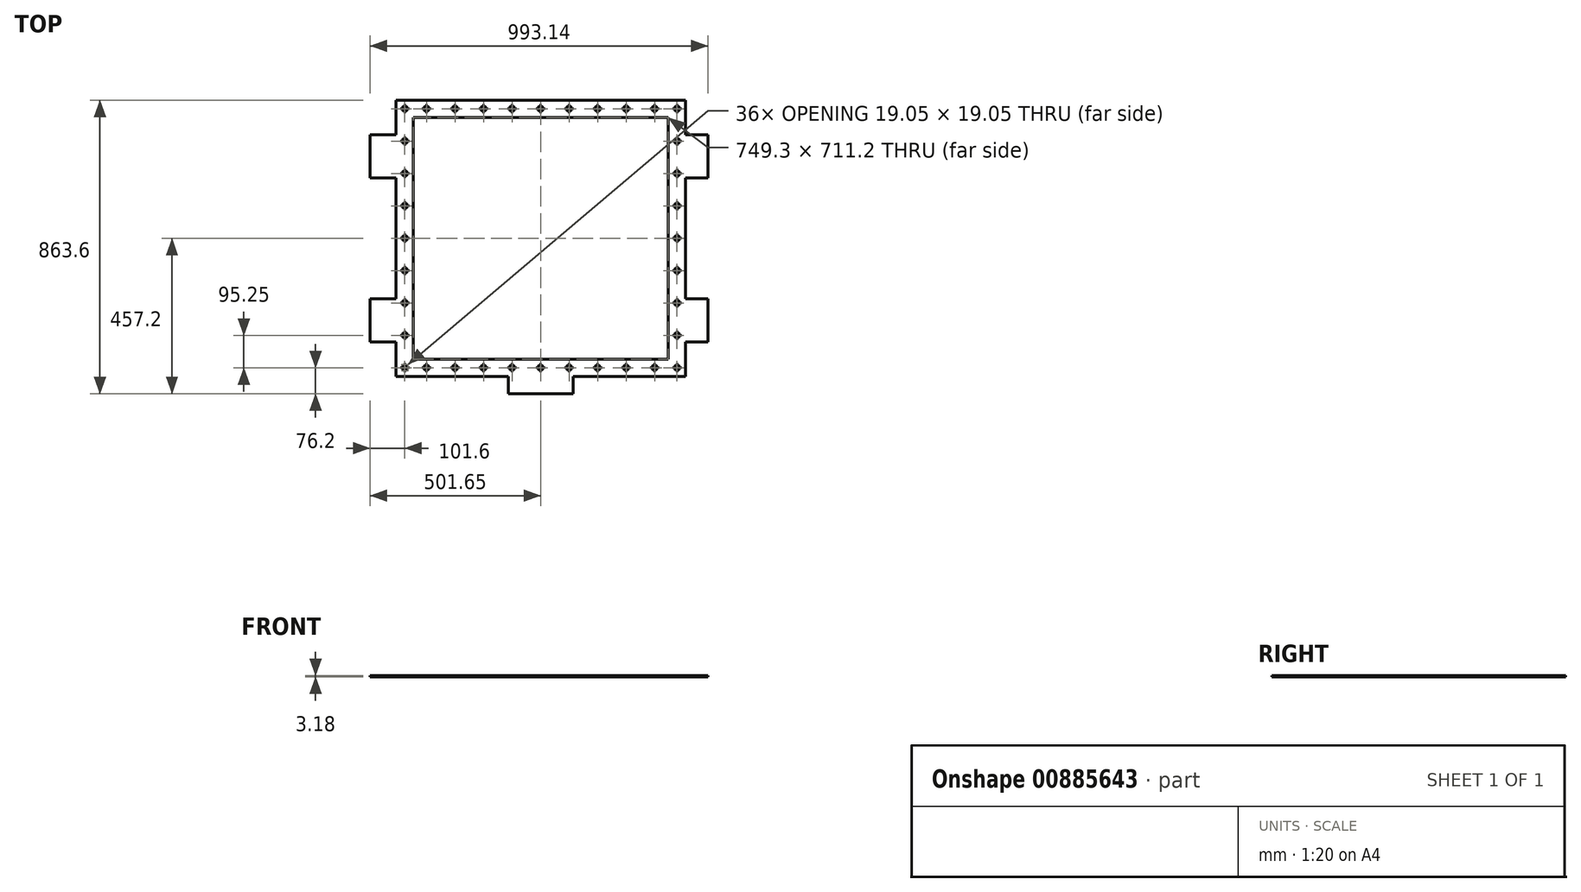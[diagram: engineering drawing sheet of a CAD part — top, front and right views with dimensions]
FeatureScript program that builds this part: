
annotation { "Feature Type Name" : "Feature", "Feature Type Description" : "" }
export const myFeature = defineFeature(function(context is Context, id is Id, definition is map)
    precondition{}
    {
        {
            var Q0;
            Q0=qCreatedBy(makeId("Top.planeOp"),FACE);
            var sketch = newSketch(context, id + "F0", { "sketchPlane" : qUnion([Q0])});
            skLineSegment(sketch, "E0.bottom", {"start": v(374.65, 355.6) * mm, "end": v(-374.65, 355.6) * mm});
            skLineSegment(sketch, "E0.top", {"start": v(374.65, -355.6) * mm, "end": v(-374.65, -355.6) * mm});
            skLineSegment(sketch, "E0.left", {"start": v(374.65, 355.6) * mm, "end": v(374.65, -355.6) * mm});
            skLineSegment(sketch, "E0.right", {"start": v(-374.65, 355.6) * mm, "end": v(-374.65, -355.6) * mm});
            skPoint(sketch, "E0.middle", {"position": v(0, 0) * mm});
            skLineSegment(sketch, "E1.bottom", {"start": v(425.45, 406.4) * mm, "end": v(-425.45, 406.4) * mm});
            skLineSegment(sketch, "E1.top", {"start": v(425.45, -406.4) * mm, "end": v(95.25, -406.4) * mm});
            skLineSegment(sketch, "E1.left", {"start": v(425.45, 406.4) * mm, "end": v(425.45, 304.8) * mm});
            skLineSegment(sketch, "E1.right", {"start": v(-425.45, 406.4) * mm, "end": v(-425.45, 304.8) * mm});
            skLineSegment(sketch, "E2.bottom", {"start": v(-425.45, 304.8) * mm, "end": v(-501.65, 304.8) * mm});
            skLineSegment(sketch, "E2.top", {"start": v(-425.45, 177.8) * mm, "end": v(-501.65, 177.8) * mm});
            skLineSegment(sketch, "E2.right", {"start": v(-501.65, 304.8) * mm, "end": v(-501.65, 177.8) * mm});
            skLineSegment(sketch, "E3.bottom", {"start": v(-425.45, -177.8) * mm, "end": v(-501.65, -177.8) * mm});
            skLineSegment(sketch, "E3.top", {"start": v(-425.45, -304.8) * mm, "end": v(-501.65, -304.8) * mm});
            skLineSegment(sketch, "E3.right", {"start": v(-501.65, -177.8) * mm, "end": v(-501.65, -304.8) * mm});
            skLineSegment(sketch, "E4.trimOffspring", {"start": v(-425.45, 177.8) * mm, "end": v(-425.45, -177.8) * mm});
            skLineSegment(sketch, "E5.trimOffspring", {"start": v(-425.45, -304.8) * mm, "end": v(-425.45, -406.4) * mm});
            skLineSegment(sketch, "E6.bottom", {"start": v(425.45, 304.8) * mm, "end": v(491.5, 304.8) * mm});
            skLineSegment(sketch, "E6.top", {"start": v(425.45, 177.8) * mm, "end": v(491.5, 177.8) * mm});
            skLineSegment(sketch, "E6.right", {"start": v(491.5, 304.8) * mm, "end": v(491.5, 177.8) * mm});
            skLineSegment(sketch, "E7.bottom", {"start": v(425.45, -177.8) * mm, "end": v(491.5, -177.8) * mm});
            skLineSegment(sketch, "E7.top", {"start": v(425.45, -304.8) * mm, "end": v(491.5, -304.8) * mm});
            skLineSegment(sketch, "E7.right", {"start": v(491.5, -177.8) * mm, "end": v(491.5, -304.8) * mm});
            skLineSegment(sketch, "E8.trimOffspring", {"start": v(425.45, 177.8) * mm, "end": v(425.45, -177.8) * mm});
            skLineSegment(sketch, "E9.trimOffspring", {"start": v(425.45, -304.8) * mm, "end": v(425.45, -406.4) * mm});
            skLineSegment(sketch, "E10.top", {"start": v(95.25, -457.2) * mm, "end": v(-95.25, -457.2) * mm});
            skLineSegment(sketch, "E10.left", {"start": v(95.25, -406.4) * mm, "end": v(95.25, -457.2) * mm});
            skLineSegment(sketch, "E10.right", {"start": v(-95.25, -406.4) * mm, "end": v(-95.25, -457.2) * mm});
            skPoint(sketch, "E10.middle", {"position": v(0, -431.8) * mm});
            skLineSegment(sketch, "E11.trimOffspring", {"start": v(-95.25, -406.4) * mm, "end": v(-425.45, -406.4) * mm});
            skSolve(sketch);
        }
        {
            var Q0;
            Q0=makeQuery(id+"F0.imprint","IMPRINT",FACE,{"disambiguationData":[TD([[makeQuery(id+"F0.imprint","IMPRINT",EDGE,{"derivedFrom":sQuery(id+"F0.wireOp",EDGE,"E0.bottom")}),-1.0]])]});
            extrude(context, id + "F1", {"entities" : qUnion([Q0]), "depth" : 3.17 * mm, "offsetDistance" : 25.4 * mm});
        }
        {
            var Q0;
            Q0=makeQuery(id+"F1.opExtrude","CAP_FACE",FACE,{"disambiguationData":[OSD([sQuery(id+"F0.wireOp",EDGE,"E0.bottom"),sQuery(id+"F0.wireOp",EDGE,"E0.top"),sQuery(id+"F0.wireOp",EDGE,"E0.left"),sQuery(id+"F0.wireOp",EDGE,"E0.right"),sQuery(id+"F0.wireOp",EDGE,"E1.bottom"),sQuery(id+"F0.wireOp",EDGE,"E1.top"),sQuery(id+"F0.wireOp",EDGE,"E1.left"),sQuery(id+"F0.wireOp",EDGE,"E1.right"),sQuery(id+"F0.wireOp",EDGE,"E2.bottom"),sQuery(id+"F0.wireOp",EDGE,"E2.top"),sQuery(id+"F0.wireOp",EDGE,"E2.right"),sQuery(id+"F0.wireOp",EDGE,"E3.bottom"),sQuery(id+"F0.wireOp",EDGE,"E3.top"),sQuery(id+"F0.wireOp",EDGE,"E3.right"),sQuery(id+"F0.wireOp",EDGE,"E4.trimOffspring"),sQuery(id+"F0.wireOp",EDGE,"E5.trimOffspring"),sQuery(id+"F0.wireOp",EDGE,"E6.bottom"),sQuery(id+"F0.wireOp",EDGE,"E6.top"),sQuery(id+"F0.wireOp",EDGE,"E6.right"),sQuery(id+"F0.wireOp",EDGE,"E7.bottom"),sQuery(id+"F0.wireOp",EDGE,"E7.top"),sQuery(id+"F0.wireOp",EDGE,"E7.right"),sQuery(id+"F0.wireOp",EDGE,"E8.trimOffspring"),sQuery(id+"F0.wireOp",EDGE,"E9.trimOffspring"),sQuery(id+"F0.wireOp",EDGE,"E10.top"),sQuery(id+"F0.wireOp",EDGE,"E10.left"),sQuery(id+"F0.wireOp",EDGE,"E10.right"),sQuery(id+"F0.wireOp",EDGE,"E11.trimOffspring")])],"isStart":false});
            var sketch = newSketch(context, id + "F2", { "sketchPlane" : qUnion([Q0])});
            skLineSegment(sketch, "E12", {"start": v(-400.05, 406.4) * mm, "end": v(-400.05, -406.4) * mm, "construction": true});
            skLineSegment(sketch, "E13", {"start": v(-425.45, 0) * mm, "end": v(425.45, 0) * mm, "construction": true});
            skLineSegment(sketch, "E14.bottom", {"start": v(-396.88, 9.52) * mm, "end": v(-403.23, 9.52) * mm});
            skLineSegment(sketch, "E14.top", {"start": v(-396.88, -9.53) * mm, "end": v(-403.23, -9.53) * mm});
            skLineSegment(sketch, "E14.left", {"start": v(-396.88, 9.52) * mm, "end": v(-396.88, 3.17) * mm});
            skLineSegment(sketch, "E14.right", {"start": v(-403.23, 9.52) * mm, "end": v(-403.23, 3.17) * mm});
            skPoint(sketch, "E14.middle", {"position": v(-400.05, 0) * mm});
            skLineSegment(sketch, "E15.bottom", {"start": v(-390.53, 3.17) * mm, "end": v(-396.88, 3.17) * mm});
            skLineSegment(sketch, "E15.top", {"start": v(-390.53, -3.18) * mm, "end": v(-396.88, -3.18) * mm});
            skLineSegment(sketch, "E15.left", {"start": v(-390.53, 3.17) * mm, "end": v(-390.53, -3.18) * mm});
            skLineSegment(sketch, "E15.right", {"start": v(-409.58, 3.17) * mm, "end": v(-409.58, -3.18) * mm});
            skLineSegment(sketch, "E16.trimOffspring", {"start": v(-403.23, 3.17) * mm, "end": v(-409.58, 3.17) * mm});
            skLineSegment(sketch, "E17.trimOffspring", {"start": v(-403.23, -3.18) * mm, "end": v(-403.23, -9.53) * mm});
            skLineSegment(sketch, "E18.trimOffspring", {"start": v(-396.88, -3.18) * mm, "end": v(-396.88, -9.53) * mm});
            skLineSegment(sketch, "E19.trimOffspring", {"start": v(-403.23, -3.18) * mm, "end": v(-409.58, -3.18) * mm});
            skLineSegment(sketch, "E20.0.1.0", {"start": v(-396.88, 92.07) * mm, "end": v(-396.88, 85.72) * mm});
            skLineSegment(sketch, "E20.0.1.1", {"start": v(-390.53, 92.07) * mm, "end": v(-396.88, 92.07) * mm});
            skLineSegment(sketch, "E20.0.1.2", {"start": v(-390.53, 98.42) * mm, "end": v(-396.88, 98.42) * mm});
            skLineSegment(sketch, "E20.0.1.3", {"start": v(-390.53, 98.42) * mm, "end": v(-390.53, 92.07) * mm});
            skLineSegment(sketch, "E20.0.1.4", {"start": v(-403.23, 92.07) * mm, "end": v(-403.23, 85.72) * mm});
            skLineSegment(sketch, "E20.0.1.5", {"start": v(-403.23, 92.07) * mm, "end": v(-409.58, 92.07) * mm});
            skLineSegment(sketch, "E20.0.1.6", {"start": v(-409.58, 98.42) * mm, "end": v(-409.58, 92.07) * mm});
            skPoint(sketch, "E20.0.1.7", {"position": v(-400.05, 95.25) * mm});
            skLineSegment(sketch, "E20.0.1.8", {"start": v(-403.23, 98.42) * mm, "end": v(-409.58, 98.42) * mm});
            skLineSegment(sketch, "E20.0.1.9", {"start": v(-396.88, 85.72) * mm, "end": v(-403.23, 85.72) * mm});
            skPoint(sketch, "E20.0.1.10", {"position": v(-400.05, 95.25) * mm});
            skLineSegment(sketch, "E20.0.1.11", {"start": v(-403.23, 104.77) * mm, "end": v(-403.23, 98.42) * mm});
            skLineSegment(sketch, "E20.0.1.12", {"start": v(-396.88, 104.77) * mm, "end": v(-403.23, 104.77) * mm});
            skLineSegment(sketch, "E20.0.1.13", {"start": v(-396.88, 104.77) * mm, "end": v(-396.88, 98.42) * mm});
            skLineSegment(sketch, "E20.0.2.0", {"start": v(-396.88, 187.32) * mm, "end": v(-396.88, 180.97) * mm});
            skLineSegment(sketch, "E20.0.2.1", {"start": v(-390.53, 187.32) * mm, "end": v(-396.88, 187.32) * mm});
            skLineSegment(sketch, "E20.0.2.2", {"start": v(-390.53, 193.67) * mm, "end": v(-396.88, 193.67) * mm});
            skLineSegment(sketch, "E20.0.2.3", {"start": v(-390.53, 193.67) * mm, "end": v(-390.53, 187.32) * mm});
            skLineSegment(sketch, "E20.0.2.4", {"start": v(-403.23, 187.32) * mm, "end": v(-403.23, 180.97) * mm});
            skLineSegment(sketch, "E20.0.2.5", {"start": v(-403.23, 187.32) * mm, "end": v(-409.58, 187.32) * mm});
            skLineSegment(sketch, "E20.0.2.6", {"start": v(-409.58, 193.67) * mm, "end": v(-409.58, 187.32) * mm});
            skPoint(sketch, "E20.0.2.7", {"position": v(-400.05, 190.5) * mm});
            skLineSegment(sketch, "E20.0.2.8", {"start": v(-403.23, 193.67) * mm, "end": v(-409.58, 193.67) * mm});
            skLineSegment(sketch, "E20.0.2.9", {"start": v(-396.88, 180.97) * mm, "end": v(-403.23, 180.97) * mm});
            skPoint(sketch, "E20.0.2.10", {"position": v(-400.05, 190.5) * mm});
            skLineSegment(sketch, "E20.0.2.11", {"start": v(-403.23, 200.02) * mm, "end": v(-403.23, 193.67) * mm});
            skLineSegment(sketch, "E20.0.2.12", {"start": v(-396.88, 200.02) * mm, "end": v(-403.23, 200.02) * mm});
            skLineSegment(sketch, "E20.0.2.13", {"start": v(-396.88, 200.02) * mm, "end": v(-396.88, 193.67) * mm});
            skLineSegment(sketch, "E20.0.3.0", {"start": v(-396.88, 282.57) * mm, "end": v(-396.88, 276.22) * mm});
            skLineSegment(sketch, "E20.0.3.1", {"start": v(-390.53, 282.57) * mm, "end": v(-396.88, 282.57) * mm});
            skLineSegment(sketch, "E20.0.3.2", {"start": v(-390.53, 288.92) * mm, "end": v(-396.88, 288.92) * mm});
            skLineSegment(sketch, "E20.0.3.3", {"start": v(-390.53, 288.92) * mm, "end": v(-390.53, 282.57) * mm});
            skLineSegment(sketch, "E20.0.3.4", {"start": v(-403.23, 282.57) * mm, "end": v(-403.23, 276.22) * mm});
            skLineSegment(sketch, "E20.0.3.5", {"start": v(-403.23, 282.57) * mm, "end": v(-409.58, 282.57) * mm});
            skLineSegment(sketch, "E20.0.3.6", {"start": v(-409.58, 288.92) * mm, "end": v(-409.58, 282.57) * mm});
            skPoint(sketch, "E20.0.3.7", {"position": v(-400.05, 285.75) * mm});
            skLineSegment(sketch, "E20.0.3.8", {"start": v(-403.23, 288.92) * mm, "end": v(-409.58, 288.92) * mm});
            skLineSegment(sketch, "E20.0.3.9", {"start": v(-396.88, 276.22) * mm, "end": v(-403.23, 276.22) * mm});
            skPoint(sketch, "E20.0.3.10", {"position": v(-400.05, 285.75) * mm});
            skLineSegment(sketch, "E20.0.3.11", {"start": v(-403.23, 295.27) * mm, "end": v(-403.23, 288.92) * mm});
            skLineSegment(sketch, "E20.0.3.12", {"start": v(-396.88, 295.27) * mm, "end": v(-403.23, 295.27) * mm});
            skLineSegment(sketch, "E20.0.3.13", {"start": v(-396.88, 295.27) * mm, "end": v(-396.88, 288.92) * mm});
            skLineSegment(sketch, "E20.0.4.0", {"start": v(-396.88, 377.82) * mm, "end": v(-396.88, 371.47) * mm});
            skLineSegment(sketch, "E20.0.4.1", {"start": v(-390.53, 377.82) * mm, "end": v(-396.88, 377.82) * mm});
            skLineSegment(sketch, "E20.0.4.2", {"start": v(-390.53, 384.17) * mm, "end": v(-396.88, 384.17) * mm});
            skLineSegment(sketch, "E20.0.4.3", {"start": v(-390.53, 384.17) * mm, "end": v(-390.53, 377.82) * mm});
            skLineSegment(sketch, "E20.0.4.4", {"start": v(-403.23, 377.82) * mm, "end": v(-403.23, 371.47) * mm});
            skLineSegment(sketch, "E20.0.4.5", {"start": v(-403.23, 377.82) * mm, "end": v(-409.58, 377.82) * mm});
            skLineSegment(sketch, "E20.0.4.6", {"start": v(-409.58, 384.17) * mm, "end": v(-409.58, 377.82) * mm});
            skPoint(sketch, "E20.0.4.7", {"position": v(-400.05, 381) * mm});
            skLineSegment(sketch, "E20.0.4.8", {"start": v(-403.23, 384.17) * mm, "end": v(-409.58, 384.17) * mm});
            skLineSegment(sketch, "E20.0.4.9", {"start": v(-396.88, 371.47) * mm, "end": v(-403.23, 371.47) * mm});
            skPoint(sketch, "E20.0.4.10", {"position": v(-400.05, 381) * mm});
            skLineSegment(sketch, "E20.0.4.11", {"start": v(-403.23, 390.52) * mm, "end": v(-403.23, 384.17) * mm});
            skLineSegment(sketch, "E20.0.4.12", {"start": v(-396.88, 390.52) * mm, "end": v(-403.23, 390.52) * mm});
            skLineSegment(sketch, "E20.0.4.13", {"start": v(-396.88, 390.52) * mm, "end": v(-396.88, 384.17) * mm});
            skLineSegment(sketch, "E20.direction1", {"start": v(-403.23, -9.53) * mm, "end": v(-403.23, -9.53) * mm});
            skLineSegment(sketch, "E20.direction2", {"start": v(-403.23, -9.53) * mm, "end": v(-403.23, 85.72) * mm, "construction": true});
            skLineSegment(sketch, "E21.0.1.0", {"start": v(-403.23, -92.08) * mm, "end": v(-409.58, -92.08) * mm});
            skLineSegment(sketch, "E21.0.1.1", {"start": v(-409.58, -92.08) * mm, "end": v(-409.58, -98.43) * mm});
            skLineSegment(sketch, "E21.0.1.2", {"start": v(-403.23, -98.43) * mm, "end": v(-403.23, -104.78) * mm});
            skLineSegment(sketch, "E21.0.1.3", {"start": v(-396.88, -98.43) * mm, "end": v(-396.88, -104.78) * mm});
            skLineSegment(sketch, "E21.0.1.4", {"start": v(-390.53, -92.08) * mm, "end": v(-396.88, -92.08) * mm});
            skLineSegment(sketch, "E21.0.1.5", {"start": v(-390.53, -98.43) * mm, "end": v(-396.88, -98.43) * mm});
            skLineSegment(sketch, "E21.0.1.6", {"start": v(-390.53, -92.08) * mm, "end": v(-390.53, -98.43) * mm});
            skLineSegment(sketch, "E21.0.1.7", {"start": v(-403.23, -98.43) * mm, "end": v(-409.58, -98.43) * mm});
            skLineSegment(sketch, "E21.0.1.8", {"start": v(-396.88, -85.73) * mm, "end": v(-403.23, -85.73) * mm});
            skLineSegment(sketch, "E21.0.1.9", {"start": v(-396.88, -104.78) * mm, "end": v(-403.23, -104.78) * mm});
            skLineSegment(sketch, "E21.0.1.10", {"start": v(-396.88, -85.73) * mm, "end": v(-396.88, -92.08) * mm});
            skLineSegment(sketch, "E21.0.1.11", {"start": v(-403.23, -85.73) * mm, "end": v(-403.23, -92.08) * mm});
            skPoint(sketch, "E21.0.1.12", {"position": v(-400.05, -95.25) * mm});
            skPoint(sketch, "E21.0.1.13", {"position": v(-400.05, -95.25) * mm});
            skLineSegment(sketch, "E21.0.2.0", {"start": v(-403.23, -187.33) * mm, "end": v(-409.58, -187.33) * mm});
            skLineSegment(sketch, "E21.0.2.1", {"start": v(-409.58, -187.33) * mm, "end": v(-409.58, -193.68) * mm});
            skLineSegment(sketch, "E21.0.2.2", {"start": v(-403.23, -193.68) * mm, "end": v(-403.23, -200.03) * mm});
            skLineSegment(sketch, "E21.0.2.3", {"start": v(-396.88, -193.68) * mm, "end": v(-396.88, -200.03) * mm});
            skLineSegment(sketch, "E21.0.2.4", {"start": v(-390.53, -187.33) * mm, "end": v(-396.88, -187.33) * mm});
            skLineSegment(sketch, "E21.0.2.5", {"start": v(-390.53, -193.68) * mm, "end": v(-396.88, -193.68) * mm});
            skLineSegment(sketch, "E21.0.2.6", {"start": v(-390.53, -187.33) * mm, "end": v(-390.53, -193.68) * mm});
            skLineSegment(sketch, "E21.0.2.7", {"start": v(-403.23, -193.68) * mm, "end": v(-409.58, -193.68) * mm});
            skLineSegment(sketch, "E21.0.2.8", {"start": v(-396.88, -180.98) * mm, "end": v(-403.23, -180.98) * mm});
            skLineSegment(sketch, "E21.0.2.9", {"start": v(-396.88, -200.03) * mm, "end": v(-403.23, -200.03) * mm});
            skLineSegment(sketch, "E21.0.2.10", {"start": v(-396.88, -180.98) * mm, "end": v(-396.88, -187.33) * mm});
            skLineSegment(sketch, "E21.0.2.11", {"start": v(-403.23, -180.98) * mm, "end": v(-403.23, -187.33) * mm});
            skPoint(sketch, "E21.0.2.12", {"position": v(-400.05, -190.5) * mm});
            skPoint(sketch, "E21.0.2.13", {"position": v(-400.05, -190.5) * mm});
            skLineSegment(sketch, "E21.0.3.0", {"start": v(-403.23, -282.58) * mm, "end": v(-409.58, -282.58) * mm});
            skLineSegment(sketch, "E21.0.3.1", {"start": v(-409.58, -282.58) * mm, "end": v(-409.58, -288.93) * mm});
            skLineSegment(sketch, "E21.0.3.2", {"start": v(-403.23, -288.93) * mm, "end": v(-403.23, -295.28) * mm});
            skLineSegment(sketch, "E21.0.3.3", {"start": v(-396.88, -288.93) * mm, "end": v(-396.88, -295.28) * mm});
            skLineSegment(sketch, "E21.0.3.4", {"start": v(-390.53, -282.58) * mm, "end": v(-396.88, -282.58) * mm});
            skLineSegment(sketch, "E21.0.3.5", {"start": v(-390.53, -288.93) * mm, "end": v(-396.88, -288.93) * mm});
            skLineSegment(sketch, "E21.0.3.6", {"start": v(-390.53, -282.58) * mm, "end": v(-390.53, -288.93) * mm});
            skLineSegment(sketch, "E21.0.3.7", {"start": v(-403.23, -288.93) * mm, "end": v(-409.58, -288.93) * mm});
            skLineSegment(sketch, "E21.0.3.8", {"start": v(-396.88, -276.23) * mm, "end": v(-403.23, -276.23) * mm});
            skLineSegment(sketch, "E21.0.3.9", {"start": v(-396.88, -295.28) * mm, "end": v(-403.23, -295.28) * mm});
            skLineSegment(sketch, "E21.0.3.10", {"start": v(-396.88, -276.23) * mm, "end": v(-396.88, -282.58) * mm});
            skLineSegment(sketch, "E21.0.3.11", {"start": v(-403.23, -276.23) * mm, "end": v(-403.23, -282.58) * mm});
            skPoint(sketch, "E21.0.3.12", {"position": v(-400.05, -285.75) * mm});
            skPoint(sketch, "E21.0.3.13", {"position": v(-400.05, -285.75) * mm});
            skLineSegment(sketch, "E21.0.4.0", {"start": v(-403.23, -377.83) * mm, "end": v(-409.58, -377.83) * mm});
            skLineSegment(sketch, "E21.0.4.1", {"start": v(-409.58, -377.83) * mm, "end": v(-409.58, -384.18) * mm});
            skLineSegment(sketch, "E21.0.4.2", {"start": v(-403.23, -384.18) * mm, "end": v(-403.23, -390.53) * mm});
            skLineSegment(sketch, "E21.0.4.3", {"start": v(-396.88, -384.18) * mm, "end": v(-396.88, -390.53) * mm});
            skLineSegment(sketch, "E21.0.4.4", {"start": v(-390.53, -377.83) * mm, "end": v(-396.88, -377.83) * mm});
            skLineSegment(sketch, "E21.0.4.5", {"start": v(-390.53, -384.18) * mm, "end": v(-396.88, -384.18) * mm});
            skLineSegment(sketch, "E21.0.4.6", {"start": v(-390.53, -377.83) * mm, "end": v(-390.53, -384.18) * mm});
            skLineSegment(sketch, "E21.0.4.7", {"start": v(-403.23, -384.18) * mm, "end": v(-409.58, -384.18) * mm});
            skLineSegment(sketch, "E21.0.4.8", {"start": v(-396.88, -371.48) * mm, "end": v(-403.23, -371.48) * mm});
            skLineSegment(sketch, "E21.0.4.9", {"start": v(-396.88, -390.53) * mm, "end": v(-403.23, -390.53) * mm});
            skLineSegment(sketch, "E21.0.4.10", {"start": v(-396.88, -371.48) * mm, "end": v(-396.88, -377.83) * mm});
            skLineSegment(sketch, "E21.0.4.11", {"start": v(-403.23, -371.48) * mm, "end": v(-403.23, -377.83) * mm});
            skPoint(sketch, "E21.0.4.12", {"position": v(-400.05, -381) * mm});
            skPoint(sketch, "E21.0.4.13", {"position": v(-400.05, -381) * mm});
            skLineSegment(sketch, "E21.direction1", {"start": v(-403.23, -9.53) * mm, "end": v(-377.83, -9.53) * mm, "construction": true});
            skLineSegment(sketch, "E21.direction2", {"start": v(-403.23, -9.53) * mm, "end": v(-403.23, -104.78) * mm, "construction": true});
            skLineSegment(sketch, "E22", {"start": v(0, -457.2) * mm, "end": v(0, 406.4) * mm, "construction": true});
            skLineSegment(sketch, "E23.0.4.0", {"start": v(-3.36, -377.86) * mm, "end": v(-9.7, -377.86) * mm});
            skLineSegment(sketch, "E23.0.4.1", {"start": v(-9.7, -377.86) * mm, "end": v(-9.7, -384.2) * mm});
            skLineSegment(sketch, "E23.0.4.2", {"start": v(-3.36, -384.2) * mm, "end": v(-3.36, -390.56) * mm});
            skLineSegment(sketch, "E23.0.4.3", {"start": v(3, -384.2) * mm, "end": v(3, -390.56) * mm});
            skLineSegment(sketch, "E23.0.4.4", {"start": v(9.34, -377.86) * mm, "end": v(3, -377.86) * mm});
            skLineSegment(sketch, "E23.0.4.5", {"start": v(9.34, -384.2) * mm, "end": v(3, -384.2) * mm});
            skLineSegment(sketch, "E23.0.4.6", {"start": v(9.34, -377.86) * mm, "end": v(9.34, -384.2) * mm});
            skLineSegment(sketch, "E23.0.4.7", {"start": v(-3.36, -384.2) * mm, "end": v(-9.7, -384.2) * mm});
            skLineSegment(sketch, "E23.0.4.8", {"start": v(3, -371.5) * mm, "end": v(-3.36, -371.5) * mm});
            skLineSegment(sketch, "E23.0.4.9", {"start": v(3, -390.56) * mm, "end": v(-3.36, -390.56) * mm});
            skLineSegment(sketch, "E23.0.4.10", {"start": v(3, -371.5) * mm, "end": v(3, -377.86) * mm});
            skLineSegment(sketch, "E23.0.4.11", {"start": v(-3.36, -371.5) * mm, "end": v(-3.36, -377.86) * mm});
            skPoint(sketch, "E23.0.4.12", {"position": v(-0.18, -381.03) * mm});
            skPoint(sketch, "E23.0.4.13", {"position": v(-0.18, -381.03) * mm});
            skLineSegment(sketch, "E24.1.0.0", {"start": v(80.46, -371.5) * mm, "end": v(80.46, -377.86) * mm});
            skLineSegment(sketch, "E24.1.0.1", {"start": v(93.16, -384.2) * mm, "end": v(86.81, -384.2) * mm});
            skLineSegment(sketch, "E24.1.0.2", {"start": v(86.81, -390.56) * mm, "end": v(80.46, -390.56) * mm});
            skLineSegment(sketch, "E24.1.0.3", {"start": v(86.81, -384.2) * mm, "end": v(86.81, -390.56) * mm});
            skLineSegment(sketch, "E24.1.0.4", {"start": v(93.16, -377.86) * mm, "end": v(86.81, -377.86) * mm});
            skPoint(sketch, "E24.1.0.5", {"position": v(83.64, -381.03) * mm});
            skLineSegment(sketch, "E24.1.0.6", {"start": v(80.46, -384.2) * mm, "end": v(80.46, -390.56) * mm});
            skLineSegment(sketch, "E24.1.0.7", {"start": v(86.81, -371.5) * mm, "end": v(86.81, -377.86) * mm});
            skLineSegment(sketch, "E24.1.0.8", {"start": v(86.81, -371.5) * mm, "end": v(80.46, -371.5) * mm});
            skPoint(sketch, "E24.1.0.9", {"position": v(83.64, -381.03) * mm});
            skLineSegment(sketch, "E24.1.0.10", {"start": v(80.46, -377.86) * mm, "end": v(74.11, -377.86) * mm});
            skLineSegment(sketch, "E24.1.0.11", {"start": v(93.16, -377.86) * mm, "end": v(93.16, -384.2) * mm});
            skLineSegment(sketch, "E24.1.0.12", {"start": v(80.46, -384.2) * mm, "end": v(74.11, -384.2) * mm});
            skLineSegment(sketch, "E24.1.0.13", {"start": v(74.11, -377.86) * mm, "end": v(74.11, -384.2) * mm});
            skLineSegment(sketch, "E24.2.0.0", {"start": v(164.28, -371.5) * mm, "end": v(164.28, -377.86) * mm});
            skLineSegment(sketch, "E24.2.0.1", {"start": v(176.98, -384.2) * mm, "end": v(170.63, -384.2) * mm});
            skLineSegment(sketch, "E24.2.0.2", {"start": v(170.63, -390.56) * mm, "end": v(164.28, -390.56) * mm});
            skLineSegment(sketch, "E24.2.0.3", {"start": v(170.63, -384.2) * mm, "end": v(170.63, -390.56) * mm});
            skLineSegment(sketch, "E24.2.0.4", {"start": v(176.98, -377.86) * mm, "end": v(170.63, -377.86) * mm});
            skPoint(sketch, "E24.2.0.5", {"position": v(167.46, -381.03) * mm});
            skLineSegment(sketch, "E24.2.0.6", {"start": v(164.28, -384.2) * mm, "end": v(164.28, -390.56) * mm});
            skLineSegment(sketch, "E24.2.0.7", {"start": v(170.63, -371.5) * mm, "end": v(170.63, -377.86) * mm});
            skLineSegment(sketch, "E24.2.0.8", {"start": v(170.63, -371.5) * mm, "end": v(164.28, -371.5) * mm});
            skPoint(sketch, "E24.2.0.9", {"position": v(167.46, -381.03) * mm});
            skLineSegment(sketch, "E24.2.0.10", {"start": v(164.28, -377.86) * mm, "end": v(157.93, -377.86) * mm});
            skLineSegment(sketch, "E24.2.0.11", {"start": v(176.98, -377.86) * mm, "end": v(176.98, -384.2) * mm});
            skLineSegment(sketch, "E24.2.0.12", {"start": v(164.28, -384.2) * mm, "end": v(157.93, -384.2) * mm});
            skLineSegment(sketch, "E24.2.0.13", {"start": v(157.93, -377.86) * mm, "end": v(157.93, -384.2) * mm});
            skLineSegment(sketch, "E24.3.0.0", {"start": v(248.1, -371.5) * mm, "end": v(248.1, -377.86) * mm});
            skLineSegment(sketch, "E24.3.0.1", {"start": v(260.8, -384.2) * mm, "end": v(254.45, -384.2) * mm});
            skLineSegment(sketch, "E24.3.0.2", {"start": v(254.45, -390.56) * mm, "end": v(248.1, -390.56) * mm});
            skLineSegment(sketch, "E24.3.0.3", {"start": v(254.45, -384.2) * mm, "end": v(254.45, -390.56) * mm});
            skLineSegment(sketch, "E24.3.0.4", {"start": v(260.8, -377.86) * mm, "end": v(254.45, -377.86) * mm});
            skPoint(sketch, "E24.3.0.5", {"position": v(251.28, -381.03) * mm});
            skLineSegment(sketch, "E24.3.0.6", {"start": v(248.1, -384.2) * mm, "end": v(248.1, -390.56) * mm});
            skLineSegment(sketch, "E24.3.0.7", {"start": v(254.45, -371.5) * mm, "end": v(254.45, -377.86) * mm});
            skLineSegment(sketch, "E24.3.0.8", {"start": v(254.45, -371.5) * mm, "end": v(248.1, -371.5) * mm});
            skPoint(sketch, "E24.3.0.9", {"position": v(251.28, -381.03) * mm});
            skLineSegment(sketch, "E24.3.0.10", {"start": v(248.1, -377.86) * mm, "end": v(241.75, -377.86) * mm});
            skLineSegment(sketch, "E24.3.0.11", {"start": v(260.8, -377.86) * mm, "end": v(260.8, -384.2) * mm});
            skLineSegment(sketch, "E24.3.0.12", {"start": v(248.1, -384.2) * mm, "end": v(241.75, -384.2) * mm});
            skLineSegment(sketch, "E24.3.0.13", {"start": v(241.75, -377.86) * mm, "end": v(241.75, -384.2) * mm});
            skLineSegment(sketch, "E24.4.0.0", {"start": v(331.92, -371.5) * mm, "end": v(331.92, -377.86) * mm});
            skLineSegment(sketch, "E24.4.0.1", {"start": v(344.62, -384.2) * mm, "end": v(338.27, -384.2) * mm});
            skLineSegment(sketch, "E24.4.0.2", {"start": v(338.27, -390.56) * mm, "end": v(331.92, -390.56) * mm});
            skLineSegment(sketch, "E24.4.0.3", {"start": v(338.27, -384.2) * mm, "end": v(338.27, -390.56) * mm});
            skLineSegment(sketch, "E24.4.0.4", {"start": v(344.62, -377.86) * mm, "end": v(338.27, -377.86) * mm});
            skPoint(sketch, "E24.4.0.5", {"position": v(335.1, -381.03) * mm});
            skLineSegment(sketch, "E24.4.0.6", {"start": v(331.92, -384.2) * mm, "end": v(331.92, -390.56) * mm});
            skLineSegment(sketch, "E24.4.0.7", {"start": v(338.27, -371.5) * mm, "end": v(338.27, -377.86) * mm});
            skLineSegment(sketch, "E24.4.0.8", {"start": v(338.27, -371.5) * mm, "end": v(331.92, -371.5) * mm});
            skPoint(sketch, "E24.4.0.9", {"position": v(335.1, -381.03) * mm});
            skLineSegment(sketch, "E24.4.0.10", {"start": v(331.92, -377.86) * mm, "end": v(325.57, -377.86) * mm});
            skLineSegment(sketch, "E24.4.0.11", {"start": v(344.62, -377.86) * mm, "end": v(344.62, -384.2) * mm});
            skLineSegment(sketch, "E24.4.0.12", {"start": v(331.92, -384.2) * mm, "end": v(325.57, -384.2) * mm});
            skLineSegment(sketch, "E24.4.0.13", {"start": v(325.57, -377.86) * mm, "end": v(325.57, -384.2) * mm});
            skLineSegment(sketch, "E24.direction1", {"start": v(-3.36, -390.56) * mm, "end": v(80.46, -390.56) * mm, "construction": true});
            skLineSegment(sketch, "E25.1.0.0", {"start": v(-80.83, -384.2) * mm, "end": v(-80.83, -390.56) * mm});
            skPoint(sketch, "E25.1.0.1", {"position": v(-84, -381.03) * mm});
            skLineSegment(sketch, "E25.1.0.2", {"start": v(-74.48, -377.86) * mm, "end": v(-80.83, -377.86) * mm});
            skLineSegment(sketch, "E25.1.0.3", {"start": v(-74.48, -384.2) * mm, "end": v(-80.83, -384.2) * mm});
            skLineSegment(sketch, "E25.1.0.4", {"start": v(-87.18, -384.2) * mm, "end": v(-87.18, -390.56) * mm});
            skLineSegment(sketch, "E25.1.0.5", {"start": v(-87.18, -371.5) * mm, "end": v(-87.18, -377.86) * mm});
            skLineSegment(sketch, "E25.1.0.6", {"start": v(-80.83, -371.5) * mm, "end": v(-87.18, -371.5) * mm});
            skLineSegment(sketch, "E25.1.0.7", {"start": v(-80.83, -390.56) * mm, "end": v(-87.18, -390.56) * mm});
            skLineSegment(sketch, "E25.1.0.8", {"start": v(-80.83, -371.5) * mm, "end": v(-80.83, -377.86) * mm});
            skPoint(sketch, "E25.1.0.9", {"position": v(-84, -381.03) * mm});
            skLineSegment(sketch, "E25.1.0.10", {"start": v(-87.18, -384.2) * mm, "end": v(-93.53, -384.2) * mm});
            skLineSegment(sketch, "E25.1.0.11", {"start": v(-87.18, -377.86) * mm, "end": v(-93.53, -377.86) * mm});
            skLineSegment(sketch, "E25.1.0.12", {"start": v(-93.53, -377.86) * mm, "end": v(-93.53, -384.2) * mm});
            skLineSegment(sketch, "E25.1.0.13", {"start": v(-74.48, -377.86) * mm, "end": v(-74.48, -384.2) * mm});
            skLineSegment(sketch, "E25.2.0.0", {"start": v(-164.65, -384.2) * mm, "end": v(-164.65, -390.56) * mm});
            skPoint(sketch, "E25.2.0.1", {"position": v(-167.82, -381.03) * mm});
            skLineSegment(sketch, "E25.2.0.2", {"start": v(-158.3, -377.86) * mm, "end": v(-164.65, -377.86) * mm});
            skLineSegment(sketch, "E25.2.0.3", {"start": v(-158.3, -384.2) * mm, "end": v(-164.65, -384.2) * mm});
            skLineSegment(sketch, "E25.2.0.4", {"start": v(-171, -384.2) * mm, "end": v(-171, -390.56) * mm});
            skLineSegment(sketch, "E25.2.0.5", {"start": v(-171, -371.5) * mm, "end": v(-171, -377.86) * mm});
            skLineSegment(sketch, "E25.2.0.6", {"start": v(-164.65, -371.5) * mm, "end": v(-171, -371.5) * mm});
            skLineSegment(sketch, "E25.2.0.7", {"start": v(-164.65, -390.56) * mm, "end": v(-171, -390.56) * mm});
            skLineSegment(sketch, "E25.2.0.8", {"start": v(-164.65, -371.5) * mm, "end": v(-164.65, -377.86) * mm});
            skPoint(sketch, "E25.2.0.9", {"position": v(-167.82, -381.03) * mm});
            skLineSegment(sketch, "E25.2.0.10", {"start": v(-171, -384.2) * mm, "end": v(-177.35, -384.2) * mm});
            skLineSegment(sketch, "E25.2.0.11", {"start": v(-171, -377.86) * mm, "end": v(-177.35, -377.86) * mm});
            skLineSegment(sketch, "E25.2.0.12", {"start": v(-177.35, -377.86) * mm, "end": v(-177.35, -384.2) * mm});
            skLineSegment(sketch, "E25.2.0.13", {"start": v(-158.3, -377.86) * mm, "end": v(-158.3, -384.2) * mm});
            skLineSegment(sketch, "E25.3.0.0", {"start": v(-248.47, -384.2) * mm, "end": v(-248.47, -390.56) * mm});
            skPoint(sketch, "E25.3.0.1", {"position": v(-251.64, -381.03) * mm});
            skLineSegment(sketch, "E25.3.0.2", {"start": v(-242.12, -377.86) * mm, "end": v(-248.47, -377.86) * mm});
            skLineSegment(sketch, "E25.3.0.3", {"start": v(-242.12, -384.2) * mm, "end": v(-248.47, -384.2) * mm});
            skLineSegment(sketch, "E25.3.0.4", {"start": v(-254.82, -384.2) * mm, "end": v(-254.82, -390.56) * mm});
            skLineSegment(sketch, "E25.3.0.5", {"start": v(-254.82, -371.5) * mm, "end": v(-254.82, -377.86) * mm});
            skLineSegment(sketch, "E25.3.0.6", {"start": v(-248.47, -371.5) * mm, "end": v(-254.82, -371.5) * mm});
            skLineSegment(sketch, "E25.3.0.7", {"start": v(-248.47, -390.56) * mm, "end": v(-254.82, -390.56) * mm});
            skLineSegment(sketch, "E25.3.0.8", {"start": v(-248.47, -371.5) * mm, "end": v(-248.47, -377.86) * mm});
            skPoint(sketch, "E25.3.0.9", {"position": v(-251.64, -381.03) * mm});
            skLineSegment(sketch, "E25.3.0.10", {"start": v(-254.82, -384.2) * mm, "end": v(-261.17, -384.2) * mm});
            skLineSegment(sketch, "E25.3.0.11", {"start": v(-254.82, -377.86) * mm, "end": v(-261.17, -377.86) * mm});
            skLineSegment(sketch, "E25.3.0.12", {"start": v(-261.17, -377.86) * mm, "end": v(-261.17, -384.2) * mm});
            skLineSegment(sketch, "E25.3.0.13", {"start": v(-242.12, -377.86) * mm, "end": v(-242.12, -384.2) * mm});
            skLineSegment(sketch, "E25.4.0.0", {"start": v(-332.29, -384.2) * mm, "end": v(-332.29, -390.56) * mm});
            skPoint(sketch, "E25.4.0.1", {"position": v(-335.46, -381.03) * mm});
            skLineSegment(sketch, "E25.4.0.2", {"start": v(-325.94, -377.86) * mm, "end": v(-332.29, -377.86) * mm});
            skLineSegment(sketch, "E25.4.0.3", {"start": v(-325.94, -384.2) * mm, "end": v(-332.29, -384.2) * mm});
            skLineSegment(sketch, "E25.4.0.4", {"start": v(-338.64, -384.2) * mm, "end": v(-338.64, -390.56) * mm});
            skLineSegment(sketch, "E25.4.0.5", {"start": v(-338.64, -371.5) * mm, "end": v(-338.64, -377.86) * mm});
            skLineSegment(sketch, "E25.4.0.6", {"start": v(-332.29, -371.5) * mm, "end": v(-338.64, -371.5) * mm});
            skLineSegment(sketch, "E25.4.0.7", {"start": v(-332.29, -390.56) * mm, "end": v(-338.64, -390.56) * mm});
            skLineSegment(sketch, "E25.4.0.8", {"start": v(-332.29, -371.5) * mm, "end": v(-332.29, -377.86) * mm});
            skPoint(sketch, "E25.4.0.9", {"position": v(-335.46, -381.03) * mm});
            skLineSegment(sketch, "E25.4.0.10", {"start": v(-338.64, -384.2) * mm, "end": v(-344.99, -384.2) * mm});
            skLineSegment(sketch, "E25.4.0.11", {"start": v(-338.64, -377.86) * mm, "end": v(-344.99, -377.86) * mm});
            skLineSegment(sketch, "E25.4.0.12", {"start": v(-344.99, -377.86) * mm, "end": v(-344.99, -384.2) * mm});
            skLineSegment(sketch, "E25.4.0.13", {"start": v(-325.94, -377.86) * mm, "end": v(-325.94, -384.2) * mm});
            skLineSegment(sketch, "E25.direction1", {"start": v(-3.36, -390.56) * mm, "end": v(-87.18, -390.56) * mm, "construction": true});
            skLineSegment(sketch, "E26.MirrorCS", {"start": v(86.81, 371.5) * mm, "end": v(86.81, 377.86) * mm});
            skLineSegment(sketch, "E27.MirrorCS", {"start": v(176.98, 384.2) * mm, "end": v(170.63, 384.2) * mm});
            skLineSegment(sketch, "E28.MirrorCS", {"start": v(248.1, 371.5) * mm, "end": v(248.1, 377.86) * mm});
            skLineSegment(sketch, "E29.MirrorCS", {"start": v(3, 390.56) * mm, "end": v(-3.36, 390.56) * mm});
            skLineSegment(sketch, "E30.MirrorCS", {"start": v(93.16, 377.86) * mm, "end": v(93.16, 384.2) * mm});
            skLineSegment(sketch, "E31.MirrorCS", {"start": v(-80.83, 371.5) * mm, "end": v(-80.83, 377.86) * mm});
            skLineSegment(sketch, "E32.MirrorCS", {"start": v(-254.82, 377.86) * mm, "end": v(-261.17, 377.86) * mm});
            skLineSegment(sketch, "E33.MirrorCS", {"start": v(338.27, 390.56) * mm, "end": v(331.92, 390.56) * mm});
            skLineSegment(sketch, "E34.MirrorCS", {"start": v(170.63, 371.5) * mm, "end": v(170.63, 377.86) * mm});
            skLineSegment(sketch, "E35.MirrorCS", {"start": v(-338.64, 384.2) * mm, "end": v(-338.64, 390.56) * mm});
            skLineSegment(sketch, "E36.MirrorCS", {"start": v(80.46, 377.86) * mm, "end": v(74.11, 377.86) * mm});
            skLineSegment(sketch, "E37.MirrorCS", {"start": v(164.28, 384.2) * mm, "end": v(157.93, 384.2) * mm});
            skLineSegment(sketch, "E38.MirrorCS", {"start": v(170.63, 390.56) * mm, "end": v(164.28, 390.56) * mm});
            skLineSegment(sketch, "E39.MirrorCS", {"start": v(93.16, 384.2) * mm, "end": v(86.81, 384.2) * mm});
            skLineSegment(sketch, "E40.MirrorCS", {"start": v(3, 371.5) * mm, "end": v(3, 377.86) * mm});
            skLineSegment(sketch, "E41.MirrorCS", {"start": v(260.8, 377.86) * mm, "end": v(254.45, 377.86) * mm});
            skLineSegment(sketch, "E42.MirrorCS", {"start": v(86.81, 371.5) * mm, "end": v(80.46, 371.5) * mm});
            skLineSegment(sketch, "E43.MirrorCS", {"start": v(-158.3, 377.86) * mm, "end": v(-158.3, 384.2) * mm});
            skLineSegment(sketch, "E44.MirrorCS", {"start": v(93.16, 377.86) * mm, "end": v(86.81, 377.86) * mm});
            skLineSegment(sketch, "E45.MirrorCS", {"start": v(-254.82, 384.2) * mm, "end": v(-254.82, 390.56) * mm});
            skLineSegment(sketch, "E46.MirrorCS", {"start": v(157.93, 377.86) * mm, "end": v(157.93, 384.2) * mm});
            skLineSegment(sketch, "E47.MirrorCS", {"start": v(74.11, 377.86) * mm, "end": v(74.11, 384.2) * mm});
            skLineSegment(sketch, "E48.MirrorCS", {"start": v(-3.36, 384.2) * mm, "end": v(-3.36, 390.56) * mm});
            skLineSegment(sketch, "E49.MirrorCS", {"start": v(325.57, 377.86) * mm, "end": v(325.57, 384.2) * mm});
            skLineSegment(sketch, "E50.MirrorCS", {"start": v(-74.48, 377.86) * mm, "end": v(-80.83, 377.86) * mm});
            skLineSegment(sketch, "E51.MirrorCS", {"start": v(-80.83, 390.56) * mm, "end": v(-87.18, 390.56) * mm});
            skLineSegment(sketch, "E52.MirrorCS", {"start": v(-242.12, 377.86) * mm, "end": v(-248.47, 377.86) * mm});
            skLineSegment(sketch, "E53.MirrorCS", {"start": v(-338.64, 377.86) * mm, "end": v(-344.99, 377.86) * mm});
            skLineSegment(sketch, "E54.MirrorCS", {"start": v(254.45, 371.5) * mm, "end": v(248.1, 371.5) * mm});
            skLineSegment(sketch, "E55.MirrorCS", {"start": v(-261.17, 377.86) * mm, "end": v(-261.17, 384.2) * mm});
            skLineSegment(sketch, "E56.MirrorCS", {"start": v(-338.64, 371.5) * mm, "end": v(-338.64, 377.86) * mm});
            skLineSegment(sketch, "E57.MirrorCS", {"start": v(-74.48, 384.2) * mm, "end": v(-80.83, 384.2) * mm});
            skLineSegment(sketch, "E58.MirrorCS", {"start": v(3, 384.2) * mm, "end": v(3, 390.56) * mm});
            skLineSegment(sketch, "E59.MirrorCS", {"start": v(164.28, 377.86) * mm, "end": v(157.93, 377.86) * mm});
            skLineSegment(sketch, "E60.MirrorCS", {"start": v(331.92, 384.2) * mm, "end": v(331.92, 390.56) * mm});
            skLineSegment(sketch, "E61.MirrorCS", {"start": v(260.8, 384.2) * mm, "end": v(254.45, 384.2) * mm});
            skLineSegment(sketch, "E62.MirrorCS", {"start": v(-3.36, 371.5) * mm, "end": v(-3.36, 377.86) * mm});
            skLineSegment(sketch, "E63.MirrorCS", {"start": v(-254.82, 371.5) * mm, "end": v(-254.82, 377.86) * mm});
            skLineSegment(sketch, "E64.MirrorCS", {"start": v(-332.29, 390.56) * mm, "end": v(-338.64, 390.56) * mm});
            skLineSegment(sketch, "E65.MirrorCS", {"start": v(176.98, 377.86) * mm, "end": v(170.63, 377.86) * mm});
            skLineSegment(sketch, "E66.MirrorCS", {"start": v(-248.47, 390.56) * mm, "end": v(-254.82, 390.56) * mm});
            skLineSegment(sketch, "E67.MirrorCS", {"start": v(-332.29, 384.2) * mm, "end": v(-332.29, 390.56) * mm});
            skLineSegment(sketch, "E68.MirrorCS", {"start": v(-80.83, 371.5) * mm, "end": v(-87.18, 371.5) * mm});
            skLineSegment(sketch, "E69.MirrorCS", {"start": v(338.27, 384.2) * mm, "end": v(338.27, 390.56) * mm});
            skLineSegment(sketch, "E70.MirrorCS", {"start": v(-325.94, 377.86) * mm, "end": v(-332.29, 377.86) * mm});
            skLineSegment(sketch, "E71.MirrorCS", {"start": v(170.63, 384.2) * mm, "end": v(170.63, 390.56) * mm});
            skLineSegment(sketch, "E72.MirrorCS", {"start": v(-87.18, 384.2) * mm, "end": v(-93.53, 384.2) * mm});
            skLineSegment(sketch, "E73.MirrorCS", {"start": v(241.75, 377.86) * mm, "end": v(241.75, 384.2) * mm});
            skLineSegment(sketch, "E74.MirrorCS", {"start": v(-3.36, 384.2) * mm, "end": v(-9.7, 384.2) * mm});
            skLineSegment(sketch, "E75.MirrorCS", {"start": v(-87.18, 371.5) * mm, "end": v(-87.18, 377.86) * mm});
            skLineSegment(sketch, "E76.MirrorCS", {"start": v(260.8, 377.86) * mm, "end": v(260.8, 384.2) * mm});
            skLineSegment(sketch, "E77.MirrorCS", {"start": v(-74.48, 377.86) * mm, "end": v(-74.48, 384.2) * mm});
            skLineSegment(sketch, "E78.MirrorCS", {"start": v(344.62, 384.2) * mm, "end": v(338.27, 384.2) * mm});
            skLineSegment(sketch, "E79.MirrorCS", {"start": v(80.46, 384.2) * mm, "end": v(74.11, 384.2) * mm});
            skLineSegment(sketch, "E80.MirrorCS", {"start": v(254.45, 371.5) * mm, "end": v(254.45, 377.86) * mm});
            skLineSegment(sketch, "E81.MirrorCS", {"start": v(176.98, 377.86) * mm, "end": v(176.98, 384.2) * mm});
            skLineSegment(sketch, "E82.MirrorCS", {"start": v(-242.12, 377.86) * mm, "end": v(-242.12, 384.2) * mm});
            skLineSegment(sketch, "E83.MirrorCS", {"start": v(-325.94, 384.2) * mm, "end": v(-332.29, 384.2) * mm});
            skLineSegment(sketch, "E84.MirrorCS", {"start": v(248.1, 377.86) * mm, "end": v(241.75, 377.86) * mm});
            skLineSegment(sketch, "E85.MirrorCS", {"start": v(-164.65, 384.2) * mm, "end": v(-164.65, 390.56) * mm});
            skLineSegment(sketch, "E86.MirrorCS", {"start": v(-9.7, 377.86) * mm, "end": v(-9.7, 384.2) * mm});
            skLineSegment(sketch, "E87.MirrorCS", {"start": v(164.28, 371.5) * mm, "end": v(164.28, 377.86) * mm});
            skLineSegment(sketch, "E88.MirrorCS", {"start": v(-171, 377.86) * mm, "end": v(-177.35, 377.86) * mm});
            skLineSegment(sketch, "E89.MirrorCS", {"start": v(-344.99, 377.86) * mm, "end": v(-344.99, 384.2) * mm});
            skLineSegment(sketch, "E90.MirrorCS", {"start": v(331.92, 384.2) * mm, "end": v(325.57, 384.2) * mm});
            skLineSegment(sketch, "E91.MirrorCS", {"start": v(80.46, 371.5) * mm, "end": v(80.46, 377.86) * mm});
            skLineSegment(sketch, "E92.MirrorCS", {"start": v(170.63, 371.5) * mm, "end": v(164.28, 371.5) * mm});
            skLineSegment(sketch, "E93.MirrorCS", {"start": v(-87.18, 377.86) * mm, "end": v(-93.53, 377.86) * mm});
            skLineSegment(sketch, "E94.MirrorCS", {"start": v(-242.12, 384.2) * mm, "end": v(-248.47, 384.2) * mm});
            skLineSegment(sketch, "E95.MirrorCS", {"start": v(164.28, 384.2) * mm, "end": v(164.28, 390.56) * mm});
            skLineSegment(sketch, "E96.MirrorCS", {"start": v(-254.82, 384.2) * mm, "end": v(-261.17, 384.2) * mm});
            skLineSegment(sketch, "E97.MirrorCS", {"start": v(338.27, 371.5) * mm, "end": v(338.27, 377.86) * mm});
            skLineSegment(sketch, "E98.MirrorCS", {"start": v(9.34, 384.2) * mm, "end": v(3, 384.2) * mm});
            skLineSegment(sketch, "E99.MirrorCS", {"start": v(-248.47, 384.2) * mm, "end": v(-248.47, 390.56) * mm});
            skLineSegment(sketch, "E100.MirrorCS", {"start": v(-332.29, 371.5) * mm, "end": v(-332.29, 377.86) * mm});
            skLineSegment(sketch, "E101.MirrorCS", {"start": v(-338.64, 384.2) * mm, "end": v(-344.99, 384.2) * mm});
            skLineSegment(sketch, "E102.MirrorCS", {"start": v(86.81, 384.2) * mm, "end": v(86.81, 390.56) * mm});
            skLineSegment(sketch, "E103.MirrorCS", {"start": v(-93.53, 377.86) * mm, "end": v(-93.53, 384.2) * mm});
            skLineSegment(sketch, "E104.MirrorCS", {"start": v(248.1, 384.2) * mm, "end": v(248.1, 390.56) * mm});
            skLineSegment(sketch, "E105.MirrorCS", {"start": v(9.34, 377.86) * mm, "end": v(9.34, 384.2) * mm});
            skLineSegment(sketch, "E106.MirrorCS", {"start": v(86.81, 390.56) * mm, "end": v(80.46, 390.56) * mm});
            skLineSegment(sketch, "E107.MirrorCS", {"start": v(-158.3, 377.86) * mm, "end": v(-164.65, 377.86) * mm});
            skLineSegment(sketch, "E108.MirrorCS", {"start": v(344.62, 377.86) * mm, "end": v(344.62, 384.2) * mm});
            skLineSegment(sketch, "E109.MirrorCS", {"start": v(-164.65, 371.5) * mm, "end": v(-164.65, 377.86) * mm});
            skLineSegment(sketch, "E110.MirrorCS", {"start": v(-158.3, 384.2) * mm, "end": v(-164.65, 384.2) * mm});
            skLineSegment(sketch, "E111.MirrorCS", {"start": v(-164.65, 390.56) * mm, "end": v(-171, 390.56) * mm});
            skLineSegment(sketch, "E112.MirrorCS", {"start": v(254.45, 384.2) * mm, "end": v(254.45, 390.56) * mm});
            skLineSegment(sketch, "E113.MirrorCS", {"start": v(254.45, 390.56) * mm, "end": v(248.1, 390.56) * mm});
            skLineSegment(sketch, "E114.MirrorCS", {"start": v(248.1, 384.2) * mm, "end": v(241.75, 384.2) * mm});
            skLineSegment(sketch, "E115.MirrorCS", {"start": v(-248.47, 371.5) * mm, "end": v(-254.82, 371.5) * mm});
            skLineSegment(sketch, "E116.MirrorCS", {"start": v(331.92, 377.86) * mm, "end": v(325.57, 377.86) * mm});
            skLineSegment(sketch, "E117.MirrorCS", {"start": v(-3.36, 377.86) * mm, "end": v(-9.7, 377.86) * mm});
            skLineSegment(sketch, "E118.MirrorCS", {"start": v(331.92, 371.5) * mm, "end": v(331.92, 377.86) * mm});
            skLineSegment(sketch, "E119.MirrorCS", {"start": v(-171, 371.5) * mm, "end": v(-171, 377.86) * mm});
            skLineSegment(sketch, "E120.MirrorCS", {"start": v(-248.47, 371.5) * mm, "end": v(-248.47, 377.86) * mm});
            skLineSegment(sketch, "E121.MirrorCS", {"start": v(-87.18, 384.2) * mm, "end": v(-87.18, 390.56) * mm});
            skLineSegment(sketch, "E122.MirrorCS", {"start": v(338.27, 371.5) * mm, "end": v(331.92, 371.5) * mm});
            skLineSegment(sketch, "E123.MirrorCS", {"start": v(-325.94, 377.86) * mm, "end": v(-325.94, 384.2) * mm});
            skLineSegment(sketch, "E124.MirrorCS", {"start": v(80.46, 384.2) * mm, "end": v(80.46, 390.56) * mm});
            skLineSegment(sketch, "E125.MirrorCS", {"start": v(3, 371.5) * mm, "end": v(-3.36, 371.5) * mm});
            skLineSegment(sketch, "E126.MirrorCS", {"start": v(-80.83, 384.2) * mm, "end": v(-80.83, 390.56) * mm});
            skLineSegment(sketch, "E127.MirrorCS", {"start": v(-171, 384.2) * mm, "end": v(-177.35, 384.2) * mm});
            skLineSegment(sketch, "E128.MirrorCS", {"start": v(-164.65, 371.5) * mm, "end": v(-171, 371.5) * mm});
            skLineSegment(sketch, "E129.MirrorCS", {"start": v(344.62, 377.86) * mm, "end": v(338.27, 377.86) * mm});
            skLineSegment(sketch, "E130.MirrorCS", {"start": v(9.34, 377.86) * mm, "end": v(3, 377.86) * mm});
            skLineSegment(sketch, "E131.MirrorCS", {"start": v(-177.35, 377.86) * mm, "end": v(-177.35, 384.2) * mm});
            skLineSegment(sketch, "E132.MirrorCS", {"start": v(-171, 384.2) * mm, "end": v(-171, 390.56) * mm});
            skLineSegment(sketch, "E133.MirrorCS", {"start": v(-332.29, 371.5) * mm, "end": v(-338.64, 371.5) * mm});
            skPoint(sketch, "E134.MirrorP", {"position": v(251.28, 381.03) * mm});
            skPoint(sketch, "E135.MirrorP", {"position": v(335.1, 381.03) * mm});
            skPoint(sketch, "E136.MirrorP", {"position": v(-251.64, 381.03) * mm});
            skPoint(sketch, "E137.MirrorP", {"position": v(83.64, 381.03) * mm});
            skPoint(sketch, "E138.MirrorP", {"position": v(-167.82, 381.03) * mm});
            skPoint(sketch, "E139.MirrorP", {"position": v(167.46, 381.03) * mm});
            skPoint(sketch, "E140.MirrorP", {"position": v(-0.18, 381.03) * mm});
            skPoint(sketch, "E141.MirrorP", {"position": v(-335.46, 381.03) * mm});
            skPoint(sketch, "E142.MirrorP", {"position": v(-84, 381.03) * mm});
            skLineSegment(sketch, "E143.MirrorCS", {"start": v(-3.36, 390.56) * mm, "end": v(-87.18, 390.56) * mm, "construction": true});
            skLineSegment(sketch, "E144.MirrorCS", {"start": v(-3.36, 390.56) * mm, "end": v(80.46, 390.56) * mm, "construction": true});
            skLineSegment(sketch, "E145.MirrorCS", {"start": v(390.53, -3.18) * mm, "end": v(396.88, -3.18) * mm});
            skLineSegment(sketch, "E146.MirrorCS", {"start": v(403.23, -3.18) * mm, "end": v(409.58, -3.18) * mm});
            skLineSegment(sketch, "E147.MirrorCS", {"start": v(403.23, -3.18) * mm, "end": v(403.23, -9.53) * mm});
            skLineSegment(sketch, "E148.MirrorCS", {"start": v(390.53, 3.17) * mm, "end": v(390.53, -3.18) * mm});
            skLineSegment(sketch, "E149.MirrorCS", {"start": v(396.88, -3.18) * mm, "end": v(396.88, -9.53) * mm});
            skLineSegment(sketch, "E150.MirrorCS", {"start": v(396.88, 390.52) * mm, "end": v(396.88, 384.17) * mm});
            skLineSegment(sketch, "E151.MirrorCS", {"start": v(409.58, 3.17) * mm, "end": v(409.58, -3.18) * mm});
            skLineSegment(sketch, "E152.MirrorCS", {"start": v(396.88, -9.53) * mm, "end": v(403.23, -9.53) * mm});
            skLineSegment(sketch, "E153.MirrorCS", {"start": v(403.23, 390.52) * mm, "end": v(403.23, 384.17) * mm});
            skLineSegment(sketch, "E154.MirrorCS", {"start": v(390.53, 377.82) * mm, "end": v(396.88, 377.82) * mm});
            skLineSegment(sketch, "E155.MirrorCS", {"start": v(390.53, 92.07) * mm, "end": v(396.88, 92.07) * mm});
            skLineSegment(sketch, "E156.MirrorCS", {"start": v(403.23, -98.43) * mm, "end": v(409.58, -98.43) * mm});
            skLineSegment(sketch, "E157.MirrorCS", {"start": v(409.58, 98.42) * mm, "end": v(409.58, 92.07) * mm});
            skLineSegment(sketch, "E158.MirrorCS", {"start": v(390.53, 384.17) * mm, "end": v(396.88, 384.17) * mm});
            skLineSegment(sketch, "E159.MirrorCS", {"start": v(403.23, 377.82) * mm, "end": v(409.58, 377.82) * mm});
            skLineSegment(sketch, "E160.MirrorCS", {"start": v(403.23, 377.82) * mm, "end": v(403.23, 371.47) * mm});
            skLineSegment(sketch, "E161.MirrorCS", {"start": v(390.53, 3.17) * mm, "end": v(396.88, 3.17) * mm});
            skLineSegment(sketch, "E162.MirrorCS", {"start": v(403.23, 384.17) * mm, "end": v(409.58, 384.17) * mm});
            skLineSegment(sketch, "E163.MirrorCS", {"start": v(390.53, 384.17) * mm, "end": v(390.53, 377.82) * mm});
            skLineSegment(sketch, "E164.MirrorCS", {"start": v(409.58, 384.17) * mm, "end": v(409.58, 377.82) * mm});
            skLineSegment(sketch, "E165.MirrorCS", {"start": v(390.53, 98.42) * mm, "end": v(396.88, 98.42) * mm});
            skLineSegment(sketch, "E166.MirrorCS", {"start": v(403.23, 3.17) * mm, "end": v(409.58, 3.17) * mm});
            skLineSegment(sketch, "E167.MirrorCS", {"start": v(396.88, 390.52) * mm, "end": v(403.23, 390.52) * mm});
            skLineSegment(sketch, "E168.MirrorCS", {"start": v(390.53, -98.43) * mm, "end": v(396.88, -98.43) * mm});
            skLineSegment(sketch, "E169.MirrorCS", {"start": v(396.88, 377.82) * mm, "end": v(396.88, 371.47) * mm});
            skLineSegment(sketch, "E170.MirrorCS", {"start": v(403.23, -377.83) * mm, "end": v(409.58, -377.83) * mm});
            skLineSegment(sketch, "E171.MirrorCS", {"start": v(403.23, 92.07) * mm, "end": v(409.58, 92.07) * mm});
            skLineSegment(sketch, "E172.MirrorCS", {"start": v(390.53, -92.08) * mm, "end": v(396.88, -92.08) * mm});
            skLineSegment(sketch, "E173.MirrorCS", {"start": v(403.23, -92.08) * mm, "end": v(409.58, -92.08) * mm});
            skLineSegment(sketch, "E174.MirrorCS", {"start": v(396.88, 371.47) * mm, "end": v(403.23, 371.47) * mm});
            skLineSegment(sketch, "E175.MirrorCS", {"start": v(403.23, -85.73) * mm, "end": v(403.23, -92.08) * mm});
            skLineSegment(sketch, "E176.MirrorCS", {"start": v(403.23, -384.18) * mm, "end": v(409.58, -384.18) * mm});
            skLineSegment(sketch, "E177.MirrorCS", {"start": v(396.88, 85.72) * mm, "end": v(403.23, 85.72) * mm});
            skLineSegment(sketch, "E178.MirrorCS", {"start": v(396.88, -384.18) * mm, "end": v(396.88, -390.53) * mm});
            skLineSegment(sketch, "E179.MirrorCS", {"start": v(396.88, -390.53) * mm, "end": v(403.23, -390.53) * mm});
            skLineSegment(sketch, "E180.MirrorCS", {"start": v(390.53, -377.83) * mm, "end": v(390.53, -384.18) * mm});
            skLineSegment(sketch, "E181.MirrorCS", {"start": v(403.23, -187.33) * mm, "end": v(409.58, -187.33) * mm});
            skLineSegment(sketch, "E182.MirrorCS", {"start": v(403.23, 282.57) * mm, "end": v(409.58, 282.57) * mm});
            skLineSegment(sketch, "E183.MirrorCS", {"start": v(403.23, -193.68) * mm, "end": v(403.23, -200.03) * mm});
            skLineSegment(sketch, "E184.MirrorCS", {"start": v(403.23, 104.77) * mm, "end": v(403.23, 98.42) * mm});
            skLineSegment(sketch, "E185.MirrorCS", {"start": v(396.88, -104.78) * mm, "end": v(403.23, -104.78) * mm});
            skLineSegment(sketch, "E186.MirrorCS", {"start": v(390.53, -384.18) * mm, "end": v(396.88, -384.18) * mm});
            skLineSegment(sketch, "E187.MirrorCS", {"start": v(403.23, -288.93) * mm, "end": v(409.58, -288.93) * mm});
            skLineSegment(sketch, "E188.MirrorCS", {"start": v(403.23, 187.32) * mm, "end": v(403.23, 180.97) * mm});
            skLineSegment(sketch, "E189.MirrorCS", {"start": v(396.88, 9.52) * mm, "end": v(396.88, 3.17) * mm});
            skLineSegment(sketch, "E190.MirrorCS", {"start": v(403.23, -282.58) * mm, "end": v(409.58, -282.58) * mm});
            skLineSegment(sketch, "E191.MirrorCS", {"start": v(396.88, -180.98) * mm, "end": v(396.88, -187.33) * mm});
            skLineSegment(sketch, "E192.MirrorCS", {"start": v(403.23, 9.52) * mm, "end": v(403.23, 3.17) * mm});
            skLineSegment(sketch, "E193.MirrorCS", {"start": v(403.23, 288.92) * mm, "end": v(409.58, 288.92) * mm});
            skLineSegment(sketch, "E194.MirrorCS", {"start": v(396.88, 104.77) * mm, "end": v(396.88, 98.42) * mm});
            skLineSegment(sketch, "E195.MirrorCS", {"start": v(403.23, 92.07) * mm, "end": v(403.23, 85.72) * mm});
            skLineSegment(sketch, "E196.MirrorCS", {"start": v(403.23, -384.18) * mm, "end": v(403.23, -390.53) * mm});
            skLineSegment(sketch, "E197.MirrorCS", {"start": v(396.88, -85.73) * mm, "end": v(403.23, -85.73) * mm});
            skLineSegment(sketch, "E198.MirrorCS", {"start": v(396.88, 104.77) * mm, "end": v(403.23, 104.77) * mm});
            skLineSegment(sketch, "E199.MirrorCS", {"start": v(409.58, -377.83) * mm, "end": v(409.58, -384.18) * mm});
            skLineSegment(sketch, "E200.MirrorCS", {"start": v(390.53, 187.32) * mm, "end": v(396.88, 187.32) * mm});
            skLineSegment(sketch, "E201.MirrorCS", {"start": v(409.58, 193.67) * mm, "end": v(409.58, 187.32) * mm});
            skLineSegment(sketch, "E202.MirrorCS", {"start": v(396.88, -85.73) * mm, "end": v(396.88, -92.08) * mm});
            skLineSegment(sketch, "E203.MirrorCS", {"start": v(390.53, 288.92) * mm, "end": v(396.88, 288.92) * mm});
            skLineSegment(sketch, "E204.MirrorCS", {"start": v(403.23, -98.43) * mm, "end": v(403.23, -104.78) * mm});
            skLineSegment(sketch, "E205.MirrorCS", {"start": v(396.88, 92.07) * mm, "end": v(396.88, 85.72) * mm});
            skLineSegment(sketch, "E206.MirrorCS", {"start": v(396.88, -98.43) * mm, "end": v(396.88, -104.78) * mm});
            skLineSegment(sketch, "E207.MirrorCS", {"start": v(409.58, -92.08) * mm, "end": v(409.58, -98.43) * mm});
            skLineSegment(sketch, "E208.MirrorCS", {"start": v(396.88, 9.52) * mm, "end": v(403.23, 9.52) * mm});
            skLineSegment(sketch, "E209.MirrorCS", {"start": v(390.53, -92.08) * mm, "end": v(390.53, -98.43) * mm});
            skLineSegment(sketch, "E210.MirrorCS", {"start": v(390.53, -282.58) * mm, "end": v(396.88, -282.58) * mm});
            skLineSegment(sketch, "E211.MirrorCS", {"start": v(390.53, -377.83) * mm, "end": v(396.88, -377.83) * mm});
            skLineSegment(sketch, "E212.MirrorCS", {"start": v(390.53, 98.42) * mm, "end": v(390.53, 92.07) * mm});
            skLineSegment(sketch, "E213.MirrorCS", {"start": v(403.23, 98.42) * mm, "end": v(409.58, 98.42) * mm});
            skLineSegment(sketch, "E214.MirrorCS", {"start": v(396.88, -180.98) * mm, "end": v(403.23, -180.98) * mm});
            skLineSegment(sketch, "E215.MirrorCS", {"start": v(390.53, -187.33) * mm, "end": v(396.88, -187.33) * mm});
            skLineSegment(sketch, "E216.MirrorCS", {"start": v(396.88, -276.23) * mm, "end": v(403.23, -276.23) * mm});
            skLineSegment(sketch, "E217.MirrorCS", {"start": v(403.23, 187.32) * mm, "end": v(409.58, 187.32) * mm});
            skLineSegment(sketch, "E218.MirrorCS", {"start": v(403.23, 200.02) * mm, "end": v(403.23, 193.67) * mm});
            skLineSegment(sketch, "E219.MirrorCS", {"start": v(403.23, 295.27) * mm, "end": v(403.23, 288.92) * mm});
            skLineSegment(sketch, "E220.MirrorCS", {"start": v(396.88, -288.93) * mm, "end": v(396.88, -295.28) * mm});
            skLineSegment(sketch, "E221.MirrorCS", {"start": v(396.88, 187.32) * mm, "end": v(396.88, 180.97) * mm});
            skLineSegment(sketch, "E222.MirrorCS", {"start": v(403.23, 282.57) * mm, "end": v(403.23, 276.22) * mm});
            skLineSegment(sketch, "E223.MirrorCS", {"start": v(396.88, 276.22) * mm, "end": v(403.23, 276.22) * mm});
            skLineSegment(sketch, "E224.MirrorCS", {"start": v(396.88, 282.57) * mm, "end": v(396.88, 276.22) * mm});
            skLineSegment(sketch, "E225.MirrorCS", {"start": v(403.23, -371.48) * mm, "end": v(403.23, -377.83) * mm});
            skLineSegment(sketch, "E226.MirrorCS", {"start": v(390.53, 193.67) * mm, "end": v(390.53, 187.32) * mm});
            skLineSegment(sketch, "E227.MirrorCS", {"start": v(409.58, 288.92) * mm, "end": v(409.58, 282.57) * mm});
            skPoint(sketch, "E228.MirrorP", {"position": v(400.05, 0) * mm});
            skLineSegment(sketch, "E229.MirrorCS", {"start": v(396.88, 295.27) * mm, "end": v(396.88, 288.92) * mm});
            skLineSegment(sketch, "E230.MirrorCS", {"start": v(396.88, 295.27) * mm, "end": v(403.23, 295.27) * mm});
            skPoint(sketch, "E231.MirrorP", {"position": v(400.05, 95.25) * mm});
            skLineSegment(sketch, "E232.MirrorCS", {"start": v(396.88, -276.23) * mm, "end": v(396.88, -282.58) * mm});
            skLineSegment(sketch, "E233.MirrorCS", {"start": v(390.53, 282.57) * mm, "end": v(396.88, 282.57) * mm});
            skLineSegment(sketch, "E234.MirrorCS", {"start": v(396.88, -200.03) * mm, "end": v(403.23, -200.03) * mm});
            skLineSegment(sketch, "E235.MirrorCS", {"start": v(396.88, -371.48) * mm, "end": v(396.88, -377.83) * mm});
            skLineSegment(sketch, "E236.MirrorCS", {"start": v(390.53, -282.58) * mm, "end": v(390.53, -288.93) * mm});
            skLineSegment(sketch, "E237.MirrorCS", {"start": v(403.23, -276.23) * mm, "end": v(403.23, -282.58) * mm});
            skLineSegment(sketch, "E238.MirrorCS", {"start": v(396.88, 200.02) * mm, "end": v(396.88, 193.67) * mm});
            skLineSegment(sketch, "E239.MirrorCS", {"start": v(403.23, 193.67) * mm, "end": v(409.58, 193.67) * mm});
            skLineSegment(sketch, "E240.MirrorCS", {"start": v(390.53, -187.33) * mm, "end": v(390.53, -193.68) * mm});
            skLineSegment(sketch, "E241.MirrorCS", {"start": v(390.53, -288.93) * mm, "end": v(396.88, -288.93) * mm});
            skLineSegment(sketch, "E242.MirrorCS", {"start": v(403.23, -193.68) * mm, "end": v(409.58, -193.68) * mm});
            skLineSegment(sketch, "E243.MirrorCS", {"start": v(390.53, 193.67) * mm, "end": v(396.88, 193.67) * mm});
            skLineSegment(sketch, "E244.MirrorCS", {"start": v(403.23, -288.93) * mm, "end": v(403.23, -295.28) * mm});
            skLineSegment(sketch, "E245.MirrorCS", {"start": v(396.88, 180.97) * mm, "end": v(403.23, 180.97) * mm});
            skLineSegment(sketch, "E246.MirrorCS", {"start": v(396.88, -295.28) * mm, "end": v(403.23, -295.28) * mm});
            skPoint(sketch, "E247.MirrorP", {"position": v(400.05, 381) * mm});
            skLineSegment(sketch, "E248.MirrorCS", {"start": v(390.53, -193.68) * mm, "end": v(396.88, -193.68) * mm});
            skLineSegment(sketch, "E249.MirrorCS", {"start": v(390.53, 288.92) * mm, "end": v(390.53, 282.57) * mm});
            skLineSegment(sketch, "E250.MirrorCS", {"start": v(409.58, -187.33) * mm, "end": v(409.58, -193.68) * mm});
            skLineSegment(sketch, "E251.MirrorCS", {"start": v(396.88, -193.68) * mm, "end": v(396.88, -200.03) * mm});
            skLineSegment(sketch, "E252.MirrorCS", {"start": v(396.88, -371.48) * mm, "end": v(403.23, -371.48) * mm});
            skLineSegment(sketch, "E253.MirrorCS", {"start": v(403.23, -180.98) * mm, "end": v(403.23, -187.33) * mm});
            skLineSegment(sketch, "E254.MirrorCS", {"start": v(409.58, -282.58) * mm, "end": v(409.58, -288.93) * mm});
            skLineSegment(sketch, "E255.MirrorCS", {"start": v(403.23, -9.53) * mm, "end": v(377.83, -9.53) * mm, "construction": true});
            skLineSegment(sketch, "E256.MirrorCS", {"start": v(396.88, 200.02) * mm, "end": v(403.23, 200.02) * mm});
            skPoint(sketch, "E257.MirrorP", {"position": v(400.05, 190.5) * mm});
            skPoint(sketch, "E258.MirrorP", {"position": v(400.05, -285.75) * mm});
            skPoint(sketch, "E259.MirrorP", {"position": v(400.05, 285.75) * mm});
            skPoint(sketch, "E260.MirrorP", {"position": v(400.05, -381) * mm});
            skPoint(sketch, "E261.MirrorP", {"position": v(400.05, -95.25) * mm});
            skPoint(sketch, "E262.MirrorP", {"position": v(400.05, -190.5) * mm});
            skLineSegment(sketch, "E263.MirrorCS", {"start": v(403.23, -9.53) * mm, "end": v(403.23, -9.53) * mm});
            skLineSegment(sketch, "E264.MirrorCS", {"start": v(403.23, -9.53) * mm, "end": v(403.23, -104.78) * mm, "construction": true});
            skLineSegment(sketch, "E265.MirrorCS", {"start": v(403.23, -9.53) * mm, "end": v(403.23, 85.72) * mm, "construction": true});
            skSolve(sketch);
        }
        {
            var Q0;
            Q0 = qSketchRegion(id + "F2", true);
            extrude(context, id + "F3", {"entities" : qUnion([Q0]), "operationType" : NewBodyOperationType.REMOVE, "oppositeDirection" : true, "depth" : 25.4 * mm, "offsetDistance" : 25.4 * mm});
        }
    });
